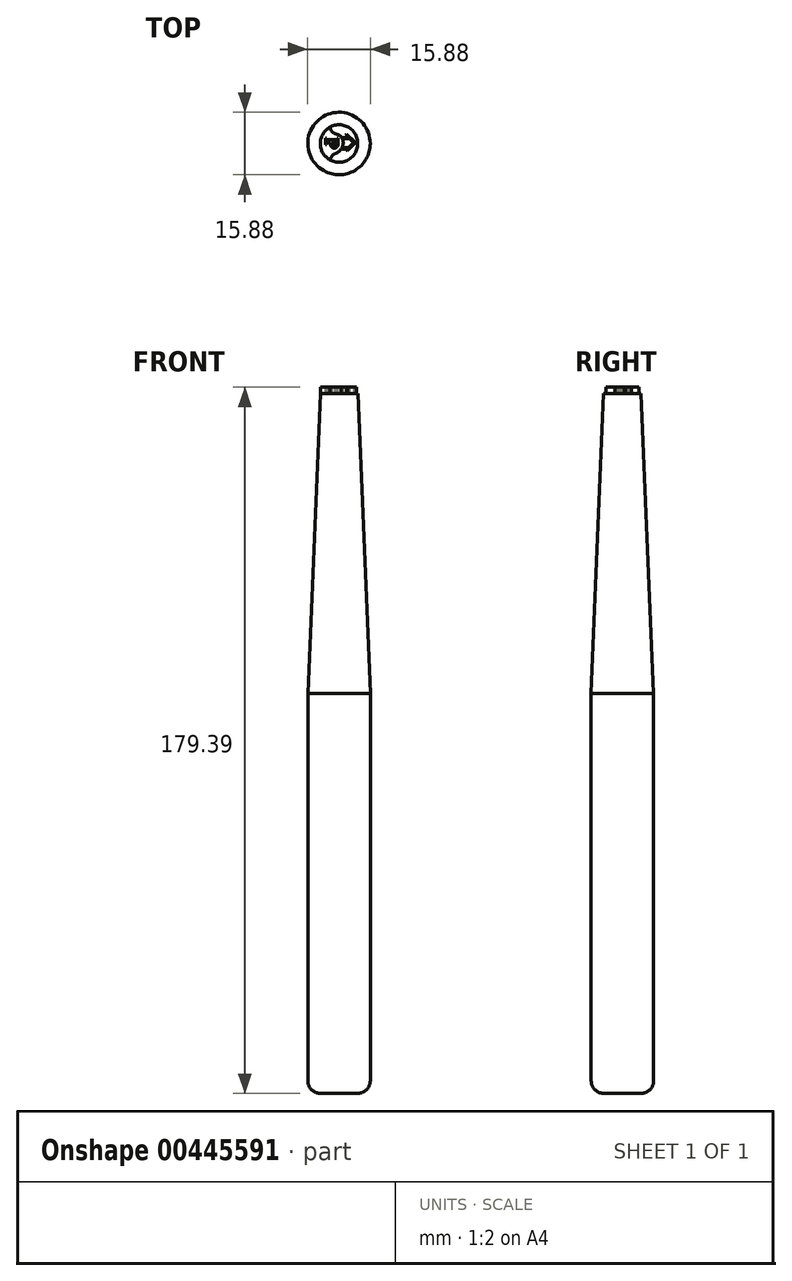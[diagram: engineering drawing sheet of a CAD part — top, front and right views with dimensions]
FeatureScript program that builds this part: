
annotation { "Feature Type Name" : "Feature", "Feature Type Description" : "" }
export const myFeature = defineFeature(function(context is Context, id is Id, definition is map)
    precondition{}
    {
        {
            var Q0;
            Q0=qCreatedBy(makeId("Top.planeOp"),FACE);
            var sketch = newSketch(context, id + "F0", { "sketchPlane" : qUnion([Q0])});
            skCircle(sketch, "E0", {"center": v(0, 0) * mm, "radius": 7.94 * mm});
            skSolve(sketch);
        }
        {
            var Q0;
            Q0=makeQuery(id+"F0.imprint","IMPRINT",FACE,{"disambiguationData":[TD([[makeQuery(id+"F0.imprint","IMPRINT",EDGE,{"derivedFrom":sQuery(id+"F0.wireOp",EDGE,"E0")}),1.0]])]});
            extrude(context, id + "F1", {"entities" : qUnion([Q0]), "depth" : 101.6 * mm});
        }
        {
            var Q0;
            Q0=makeQuery(id+"F1.opExtrude","CAP_FACE",FACE,{"disambiguationData":[OSD([sQuery(id+"F0.wireOp",EDGE,"E0")])],"isStart":false});
            cPlane(context, id + "F2", {"entities" : qUnion([Q0]), "cplaneType" : CPlaneType.OFFSET, "offset" : 76.2 * mm, "width" : 152.4 * mm, "height" : 152.4 * mm});
        }
        {
            var Q0;
            Q0=qCreatedBy(id+"F2.planeOp",FACE);
            var sketch = newSketch(context, id + "F3", { "sketchPlane" : qUnion([Q0])});
            skCircle(sketch, "E1", {"center": v(0, 0) * mm, "radius": 4.76 * mm});
            skSolve(sketch);
        }
        {
            var Q1;
            Q1=makeQuery(id+"F1.opExtrude","CAP_FACE",FACE,{"disambiguationData":[OSD([sQuery(id+"F0.wireOp",EDGE,"E0")])],"isStart":false});
            var Q2;
            Q2=makeQuery(id+"F3.imprint","IMPRINT",FACE,{"disambiguationData":[TD([[makeQuery(id+"F3.imprint","IMPRINT",EDGE,{"derivedFrom":sQuery(id+"F3.wireOp",EDGE,"E1")}),1.0]])]});
            loft(context, id + "F4", {"operationType" : NewBodyOperationType.ADD, "sheetProfilesArray" : [{ "sheetProfileEntities" : qUnion([Q1]) }, { "sheetProfileEntities" : qUnion([Q2]) }]});
        }
        {
            var Q0;
            Q0=makeQuery(id+"F4.opLoft","CAP_FACE",FACE,{"disambiguationData":[OSD([makeQuery(id+"F3.imprint","IMPRINT",FACE,{"disambiguationData":[TD([[makeQuery(id+"F3.imprint","IMPRINT",EDGE,{"derivedFrom":sQuery(id+"F3.wireOp",EDGE,"E1")}),1.0]])]})])],"isStart":true});
            var sketch = newSketch(context, id + "F5", { "sketchPlane" : qUnion([Q0])});
            skFitSpline(sketch, "E2", {"points": [v(-2.3, 4.17) * mm, v(-1.44, 2.73) * mm, v(0.19, 2) * mm, v(1.08, 0.17) * mm, v(0, -2.02) * mm, v(-1.4, -2.78) * mm, v(-2.32, -4.16) * mm], "startDerivative": vector(2.44, -9.19) * mm, "endDerivative": vector(-3.99, -11.83) * mm});
            skArc(sketch, "E3", {"start": v(-2.3, 4.17) * mm, "mid": v(-4.76, 0) * mm, "end": v(-2.32, -4.16) * mm});
            skLineSegment(sketch, "E4.bottom", {"start": v(0.67, 1.52) * mm, "end": v(2.28, 1.52) * mm});
            skLineSegment(sketch, "E4.top", {"start": v(0.86, 1.2) * mm, "end": v(2.62, 1.2) * mm});
            skLineSegment(sketch, "E5.bottom", {"start": v(0.56, -1.39) * mm, "end": v(2.14, -1.39) * mm});
            skLineSegment(sketch, "E5.top", {"start": v(0.74, -1.07) * mm, "end": v(2.44, -1.07) * mm});
            skLineSegment(sketch, "E6", {"start": v(1.7, 2.07) * mm, "end": v(2.28, 1.52) * mm});
            skLineSegment(sketch, "E7", {"start": v(3.88, 0.44) * mm, "end": v(1.9, 2.33) * mm});
            skLineSegment(sketch, "E8", {"start": v(1.9, 2.33) * mm, "end": v(1.7, 2.07) * mm});
            skLineSegment(sketch, "E9.trimOffspring", {"start": v(2.62, 1.2) * mm, "end": v(3.66, 0.21) * mm});
            skLineSegment(sketch, "E10", {"start": v(1.9, -1.65) * mm, "end": v(2.14, -1.39) * mm});
            skLineSegment(sketch, "E11", {"start": v(4.18, 0.76) * mm, "end": v(4.41, 0.54) * mm});
            skLineSegment(sketch, "E12", {"start": v(4.41, 0.54) * mm, "end": v(2.13, -1.86) * mm});
            skLineSegment(sketch, "E13", {"start": v(1.9, -1.65) * mm, "end": v(2.13, -1.86) * mm});
            skLineSegment(sketch, "E14.trimOffspring", {"start": v(2.44, -1.07) * mm, "end": v(3.66, 0.21) * mm});
            skLineSegment(sketch, "E15.trimOffspring", {"start": v(3.88, 0.44) * mm, "end": v(4.18, 0.76) * mm});
            skSolve(sketch);
        }
        {
            var Q0;
            Q0 = qSketchRegion(id + "F5", true);
            extrude(context, id + "F6", {"entities" : qUnion([Q0]), "operationType" : NewBodyOperationType.ADD, "depth" : 1.59 * mm});
        }
        {
            var Q0;
            Q0=makeQuery(id+"F1.opExtrude","CAP_EDGE",EDGE,{"disambiguationData":[OSD([sQuery(id+"F0.wireOp",EDGE,"E0")])],"isStart":true});
            fillet(context, id + "F7", {"entities" : qUnion([Q0]), "radius" : 3.17 * mm, "tangentPropagation" : true, "allowEdgeOverflow" : false});
        }
        {
            var Q0;
            Q0=makeQuery(id+"F6.opExtrude","CAP_FACE",FACE,{"disambiguationData":[OSD([sQuery(id+"F5.wireOp",EDGE,"E2"),sQuery(id+"F5.wireOp",EDGE,"E3"),sQuery(id+"F5.wireOp",EDGE,"E4.bottom"),sQuery(id+"F5.wireOp",EDGE,"E4.top"),sQuery(id+"F5.wireOp",EDGE,"E5.bottom"),sQuery(id+"F5.wireOp",EDGE,"E5.top"),sQuery(id+"F5.wireOp",EDGE,"E2"),sQuery(id+"F5.wireOp",EDGE,"E2"),sQuery(id+"F5.wireOp",EDGE,"E6"),sQuery(id+"F5.wireOp",EDGE,"E7"),sQuery(id+"F5.wireOp",EDGE,"E8"),sQuery(id+"F5.wireOp",EDGE,"E9.trimOffspring"),sQuery(id+"F5.wireOp",EDGE,"E10"),sQuery(id+"F5.wireOp",EDGE,"E11"),sQuery(id+"F5.wireOp",EDGE,"E12"),sQuery(id+"F5.wireOp",EDGE,"E13"),sQuery(id+"F5.wireOp",EDGE,"E14.trimOffspring"),sQuery(id+"F5.wireOp",EDGE,"E15.trimOffspring")])],"isStart":false});
            var sketch = newSketch(context, id + "F8", { "sketchPlane" : qUnion([Q0])});
            skText(sketch, "E16", { "text": "P", "fontName": "NotoSerif-Bold.ttf"});
            const initialGuessF8  = {"E16": [-0.0034, 0.0015, 0, -1, 0.00317]};
            skSetInitialGuess(sketch, initialGuessF8);
            skSolve(sketch);
        }
        {
            var Q0;
            Q0 = qSketchRegion(id + "F8", true);
            extrude(context, id + "F9", {"entities" : qUnion([Q0]), "operationType" : NewBodyOperationType.REMOVE, "oppositeDirection" : true, "depth" : 1.59 * mm});
        }
    });
